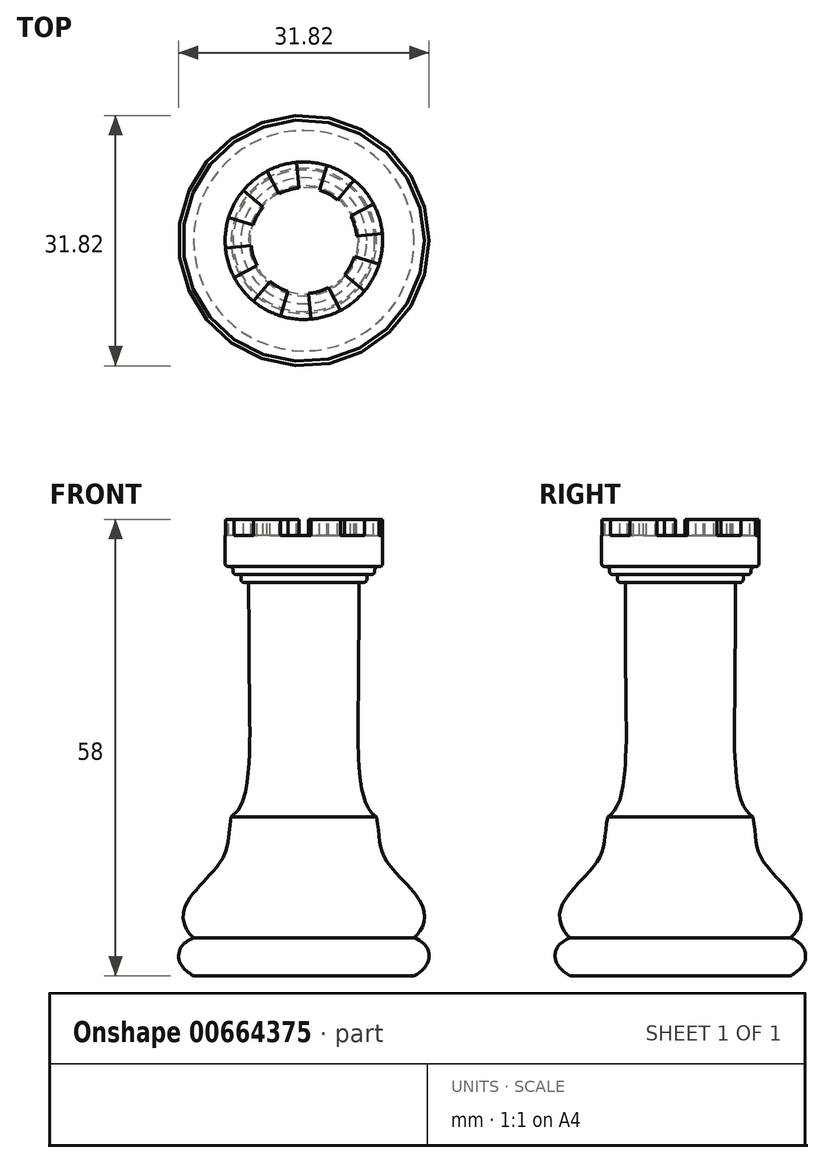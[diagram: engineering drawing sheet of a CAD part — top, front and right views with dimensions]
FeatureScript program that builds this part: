
annotation { "Feature Type Name" : "Feature", "Feature Type Description" : "" }
export const myFeature = defineFeature(function(context is Context, id is Id, definition is map)
    precondition{}
    {
        {
            var Q0;
            Q0=qCreatedBy(makeId("Front.planeOp"),FACE);
            var sketch = newSketch(context, id + "F0", { "sketchPlane" : qUnion([Q0])});
            skLineSegment(sketch, "E0", {"start": v(7.47, -35.9) * mm, "end": v(21.47, -35.9) * mm});
            skFitSpline(sketch, "E1", {"points": [v(21.47, -35.9) * mm, v(23.38, -33.28) * mm, v(21.47, -31.02) * mm], "startDerivative": vector(8.57, 5.13) * mm, "endDerivative": vector(-8.7, 3.67) * mm});
            skFitSpline(sketch, "E2", {"points": [v(21.47, -31.02) * mm, v(22.7, -27.5) * mm, v(17.9, -21.14) * mm, v(16.7, -15.66) * mm], "startDerivative": vector(9.35, 7.58) * mm, "endDerivative": vector(-4, 21.15) * mm});
            skLineSegment(sketch, "E3", {"start": v(7.47, 14.1) * mm, "end": v(7.47, -35.9) * mm});
            skLineSegment(sketch, "E4", {"start": v(14.47, 14.1) * mm, "end": v(15.47, 14.1) * mm});
            skLineSegment(sketch, "E5", {"start": v(15.47, 14.1) * mm, "end": v(15.47, 15.1) * mm});
            skLineSegment(sketch, "E6", {"start": v(15.47, 15.1) * mm, "end": v(16.47, 15.1) * mm});
            skLineSegment(sketch, "E7", {"start": v(16.47, 15.1) * mm, "end": v(16.47, 16.1) * mm});
            skLineSegment(sketch, "E8", {"start": v(16.47, 16.1) * mm, "end": v(17.47, 16.1) * mm});
            skLineSegment(sketch, "E9", {"start": v(17.47, 22.1) * mm, "end": v(7.47, 22.1) * mm});
            skLineSegment(sketch, "E10", {"start": v(7.47, 22.1) * mm, "end": v(7.47, 14.1) * mm});
            skFitSpline(sketch, "E11", {"points": [v(14.47, 14.1) * mm, v(14.47, -9.07) * mm, v(16.7, -15.66) * mm], "startDerivative": vector(0, -79.24) * mm, "endDerivative": vector(14.58, -8.1) * mm});
            skLineSegment(sketch, "E12", {"start": v(17.47, 16.1) * mm, "end": v(17.47, 22.1) * mm});
            skSolve(sketch);
        }
        {
            var Q0;
            Q0 = qSketchRegion(id + "F0", true);
            var Q1;
            Q1=sQuery(id+"F0.wireOp",EDGE,"E3");
            revolve(context, id + "F1", {"surfaceOperationType" : NewSurfaceOperationType.NEW, "entities" : qUnion([Q0]), "axis" : qUnion([Q1]), "revolveType" : RevolveType.FULL});
        }
        {
            var Q0;
            Q0=qCreatedBy(makeId("Top.planeOp"),FACE);
            cPlane(context, id + "F2", {"entities" : qUnion([Q0]), "cplaneType" : CPlaneType.OFFSET, "offset" : 24.08 * mm, "width" : 150 * mm, "height" : 150 * mm});
        }
        {
            var Q0;
            Q0=qCreatedBy(id+"F2.planeOp",FACE);
            var sketch = newSketch(context, id + "F3", { "sketchPlane" : qUnion([Q0])});
            skArc(sketch, "E13", {"start": v(2.3, 4.3) * mm, "mid": v(1.56, 3.2) * mm, "end": v(1.05, 1.99) * mm});
            skPoint(sketch, "E14.0.midPoint", {"position": v(15.16, 6.3) * mm});
            skArc(sketch, "E15", {"start": v(-2.08, 2.96) * mm, "mid": v(-2.48, 1.04) * mm, "end": v(-2.49, -0.92) * mm});
            skLineSegment(sketch, "E16", {"start": v(6.85, 6.7) * mm, "end": v(6.55, 9.96) * mm});
            skLineSegment(sketch, "E17", {"start": v(9.46, 6.42) * mm, "end": v(10.43, 9.55) * mm});
            skLineSegment(sketch, "E18", {"start": v(11.77, 5.17) * mm, "end": v(13.86, 7.7) * mm});
            skLineSegment(sketch, "E19", {"start": v(13.42, 3.13) * mm, "end": v(16.32, 4.66) * mm});
            skLineSegment(sketch, "E20", {"start": v(14.16, 0.62) * mm, "end": v(17.43, 0.92) * mm});
            skLineSegment(sketch, "E21", {"start": v(13.9, -1.99) * mm, "end": v(17.02, -2.96) * mm});
            skLineSegment(sketch, "E22", {"start": v(12.64, -4.3) * mm, "end": v(15.16, -6.4) * mm});
            skLineSegment(sketch, "E23", {"start": v(10.6, -5.95) * mm, "end": v(12.13, -8.85) * mm});
            skLineSegment(sketch, "E24", {"start": v(8.09, -6.7) * mm, "end": v(8.4, -9.96) * mm});
            skLineSegment(sketch, "E25", {"start": v(5.48, -6.42) * mm, "end": v(4.51, -9.55) * mm});
            skLineSegment(sketch, "E26", {"start": v(3.18, -5.17) * mm, "end": v(1.08, -7.7) * mm});
            skLineSegment(sketch, "E27", {"start": v(0.78, -0.62) * mm, "end": v(-2.49, -0.92) * mm});
            skLineSegment(sketch, "E28", {"start": v(1.05, 1.99) * mm, "end": v(-2.08, 2.96) * mm});
            skLineSegment(sketch, "E29", {"start": v(2.3, 4.3) * mm, "end": v(-0.22, 6.4) * mm});
            skLineSegment(sketch, "E30", {"start": v(4.34, 5.95) * mm, "end": v(2.8, 8.85) * mm});
            skLineSegment(sketch, "E31", {"start": v(-1.38, -4.66) * mm, "end": v(1.52, -3.13) * mm});
            skArc(sketch, "E32.trimOffspring", {"start": v(2.8, 8.85) * mm, "mid": v(1.17, 7.77) * mm, "end": v(-0.22, 6.4) * mm});
            skArc(sketch, "E33.trimOffspring", {"start": v(6.85, 6.7) * mm, "mid": v(5.56, 6.44) * mm, "end": v(4.34, 5.95) * mm});
            skArc(sketch, "E34.trimOffspring", {"start": v(10.43, 9.55) * mm, "mid": v(8.5, 9.95) * mm, "end": v(6.55, 9.96) * mm});
            skArc(sketch, "E35.trimOffspring", {"start": v(11.77, 5.17) * mm, "mid": v(10.67, 5.9) * mm, "end": v(9.46, 6.42) * mm});
            skArc(sketch, "E36.trimOffspring", {"start": v(16.32, 4.66) * mm, "mid": v(15.24, 6.3) * mm, "end": v(13.86, 7.7) * mm});
            skArc(sketch, "E37.trimOffspring", {"start": v(14.16, 0.62) * mm, "mid": v(13.91, 1.91) * mm, "end": v(13.42, 3.13) * mm});
            skArc(sketch, "E38.trimOffspring", {"start": v(17.02, -2.96) * mm, "mid": v(17.42, -1.04) * mm, "end": v(17.43, 0.92) * mm});
            skArc(sketch, "E39.trimOffspring", {"start": v(12.64, -4.3) * mm, "mid": v(13.38, -3.2) * mm, "end": v(13.9, -1.99) * mm});
            skArc(sketch, "E40.trimOffspring", {"start": v(12.13, -8.85) * mm, "mid": v(13.77, -7.77) * mm, "end": v(15.16, -6.4) * mm});
            skArc(sketch, "E41.trimOffspring", {"start": v(8.09, -6.7) * mm, "mid": v(9.38, -6.44) * mm, "end": v(10.6, -5.95) * mm});
            skArc(sketch, "E42.trimOffspring", {"start": v(4.51, -9.55) * mm, "mid": v(6.43, -9.95) * mm, "end": v(8.4, -9.96) * mm});
            skArc(sketch, "E43.trimOffspring", {"start": v(3.18, -5.17) * mm, "mid": v(4.27, -5.9) * mm, "end": v(5.48, -6.42) * mm});
            skArc(sketch, "E44.trimOffspring", {"start": v(-1.38, -4.66) * mm, "mid": v(-0.3, -6.3) * mm, "end": v(1.08, -7.7) * mm});
            skArc(sketch, "E45.trimOffspring", {"start": v(0.78, -0.62) * mm, "mid": v(1.03, -1.91) * mm, "end": v(1.52, -3.13) * mm});
            skSolve(sketch);
        }
        {
            var Q0;
            Q0 = qSketchRegion(id + "F3", true);
            extrude(context, id + "F4", {"entities" : qUnion([Q0]), "operationType" : NewBodyOperationType.REMOVE, "oppositeDirection" : true, "depth" : 4 * mm, "offsetDistance" : 25 * mm});
        }
        {
            var Q0;
            Q0=makeQuery(id+"F1.opRevolve","SWEPT_EDGE",EDGE,{"disambiguationData":[OSD([sQuery(id+"F0.wireOp",EDGE,"E6"),sQuery(id+"F0.wireOp",EDGE,"E7")])]});
            var Q1;
            Q1=makeQuery(id+"F1.opRevolve","SWEPT_EDGE",EDGE,{"disambiguationData":[OSD([sQuery(id+"F0.wireOp",EDGE,"E4"),sQuery(id+"F0.wireOp",EDGE,"E5")])]});
            var Q2;
            Q2=makeQuery(id+"F1.opRevolve","SWEPT_EDGE",EDGE,{"disambiguationData":[OSD([sQuery(id+"F0.wireOp",EDGE,"E8"),sQuery(id+"F0.wireOp",EDGE,"wnXNPD1H-NTGp-F3ZW-DtEV-09cMiZo2yqDI")])]});
            fillet(context, id + "F5", {"entities" : qUnion([Q0, Q1, Q2]), "radius" : .4 * mm, "tangentPropagation" : true, "allowEdgeOverflow" : false});
        }
    });
